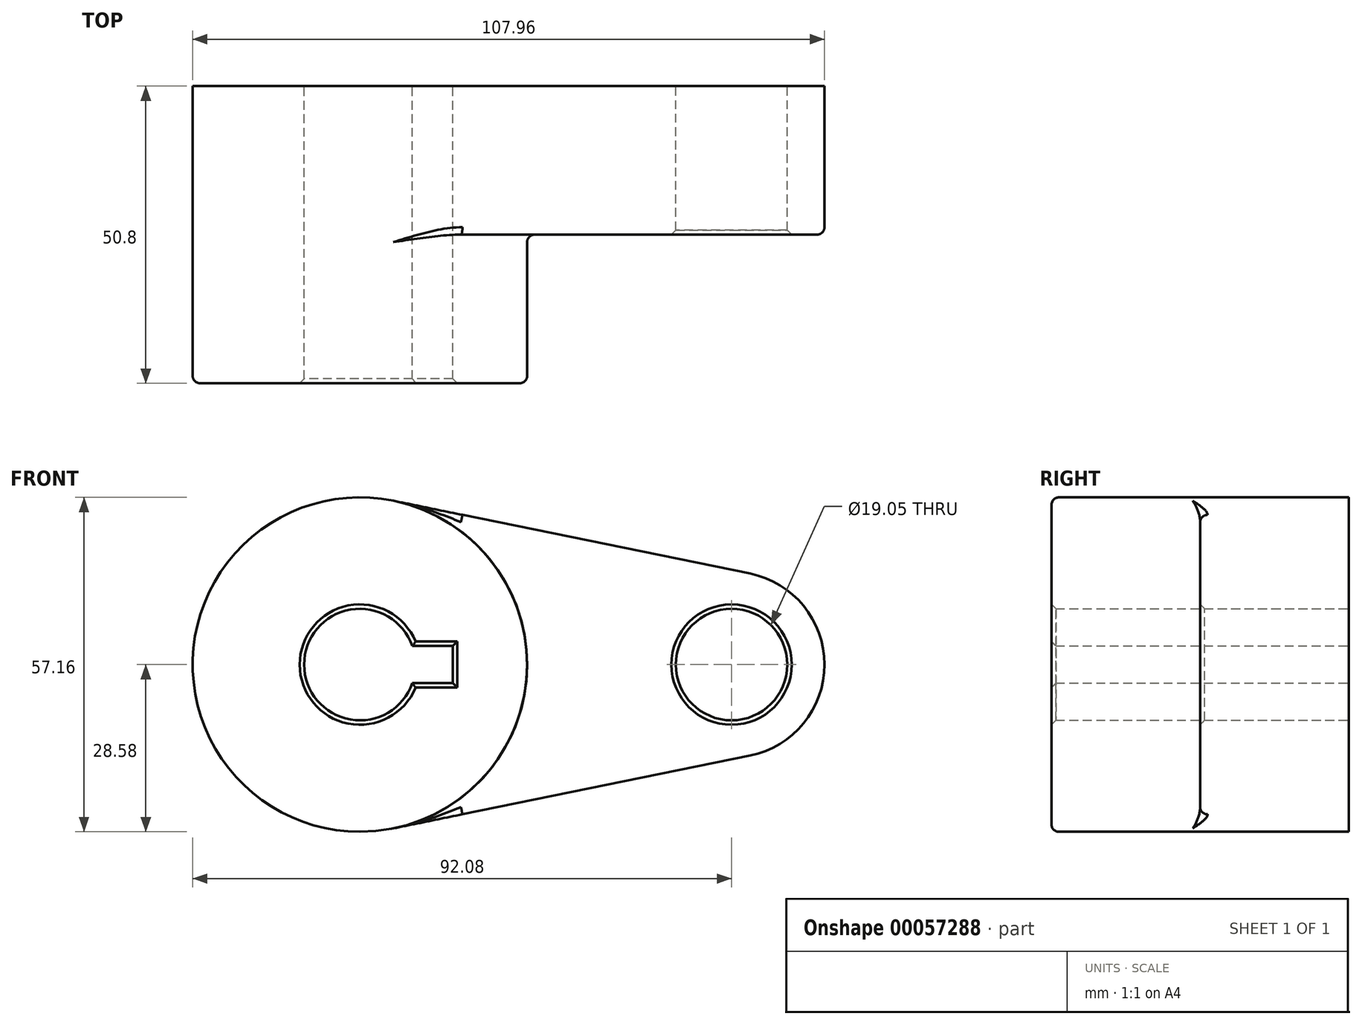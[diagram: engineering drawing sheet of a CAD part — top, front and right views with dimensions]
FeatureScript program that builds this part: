
annotation { "Feature Type Name" : "Feature", "Feature Type Description" : "" }
export const myFeature = defineFeature(function(context is Context, id is Id, definition is map)
    precondition{}
    {
        {
            var Q0;
            Q0=qCreatedBy(makeId("Front.planeOp"),FACE);
            var sketch = newSketch(context, id + "F0", { "sketchPlane" : qUnion([Q0])});
            skCircle(sketch, "E0", {"center": v(0, 0) * mm, "radius": 28.58 * mm});
            skCircle(sketch, "E1", {"center": v(63.5, 0) * mm, "radius": 15.88 * mm});
            skLineSegment(sketch, "E2", {"start": v(5.71, 28) * mm, "end": v(66.68, 15.55) * mm});
            skLineSegment(sketch, "E3", {"start": v(5.71, -28) * mm, "end": v(66.68, -15.55) * mm});
            skCircle(sketch, "E4", {"center": v(0, 0) * mm, "radius": 9.53 * mm});
            skCircle(sketch, "E5", {"center": v(63.5, 0) * mm, "radius": 9.53 * mm});
            skLineSegment(sketch, "E6.rect.bottom", {"start": v(-15.88, 3.17) * mm, "end": v(15.88, 3.17) * mm});
            skLineSegment(sketch, "E6.rect.top", {"start": v(-15.88, -3.17) * mm, "end": v(15.88, -3.17) * mm});
            skLineSegment(sketch, "E6.rect.left", {"start": v(-15.88, 3.17) * mm, "end": v(-15.88, -3.17) * mm});
            skLineSegment(sketch, "E6.rect.right", {"start": v(15.88, 3.17) * mm, "end": v(15.88, -3.17) * mm});
            skSolve(sketch);
        }
        {
            var Q0;
            {var subQ11=sQuery(id+"F0.wireOp",EDGE,"E6.rect.left");Q0=makeQuery(id+"F0.imprint","IMPRINT",FACE,{"disambiguationData":[TD([[makeQuery(id+"F0.imprint","IMPRINT",EDGE,{"derivedFrom":subQ11}),-1.0]])]});}
            var Q1;
            Q1=makeQuery(id+"F0.imprint","IMPRINT",FACE,{"disambiguationData":[TD([[makeQuery(id+"F0.imprint","IMPRINT",EDGE,{"derivedFrom":sQuery(id+"F0.wireOp",EDGE,"E5")}),-1.0]])]});
            var Q2;
            {var subQ0=sQuery(id+"F0.wireOp",EDGE,"E2");Q2=makeQuery(id+"F0.imprint","IMPRINT",FACE,{"disambiguationData":[TD([[makeQuery(id+"F0.imprint","IMPRINT",EDGE,{"derivedFrom":subQ0}),-1.0]])]});}
            var Q3;
            {var subQ5=sQuery(id+"F0.wireOp",EDGE,"E6.rect.left");Q3=makeQuery(id+"F0.imprint","IMPRINT",FACE,{"disambiguationData":[TD([[makeQuery(id+"F0.imprint","IMPRINT",EDGE,{"derivedFrom":subQ5}),1.0]])]});}
            extrude(context, id + "F1", {"entities" : qUnion([Q0, Q1, Q2, Q3]), "depth" : 25.4 * mm});
        }
        {
            var Q0;
            {var subQ11=sQuery(id+"F0.wireOp",EDGE,"E6.rect.left");Q0=makeQuery(id+"F0.imprint","IMPRINT",FACE,{"disambiguationData":[TD([[makeQuery(id+"F0.imprint","IMPRINT",EDGE,{"derivedFrom":subQ11}),-1.0]])]});}
            var Q1;
            {var subQ5=sQuery(id+"F0.wireOp",EDGE,"E6.rect.left");Q1=makeQuery(id+"F0.imprint","IMPRINT",FACE,{"disambiguationData":[TD([[makeQuery(id+"F0.imprint","IMPRINT",EDGE,{"derivedFrom":subQ5}),1.0]])]});}
            extrude(context, id + "F2", {"entities" : qUnion([Q0, Q1]), "operationType" : NewBodyOperationType.ADD, "depth" : 50.8 * mm});
        }
        {
            var Q0;
            {var subQ0=sQuery(id+"F0.wireOp",EDGE,"E0");Q0=makeQuery(id+"F2.boolean.opBoolean","INTERSECT",EDGE,{"derivedFrom":[makeQuery(id+"F1.opExtrude","CAP_FACE",FACE,{"disambiguationData":[OSD([subQ0,sQuery(id+"F0.wireOp",EDGE,"E1"),sQuery(id+"F0.wireOp",EDGE,"E2"),sQuery(id+"F0.wireOp",EDGE,"E3"),sQuery(id+"F0.wireOp",EDGE,"E4"),sQuery(id+"F0.wireOp",EDGE,"E5"),sQuery(id+"F0.wireOp",EDGE,"E6.rect.bottom"),sQuery(id+"F0.wireOp",EDGE,"E6.rect.top"),sQuery(id+"F0.wireOp",EDGE,"E6.rect.right")])],"isStart":false}),makeQuery(id+"F2.opExtrude","SWEPT_FACE",FACE,{"disambiguationData":[OSD([subQ0])]})]});}
            fillet(context, id + "F3", {"entities" : qUnion([Q0]), "radius" : 1.27 * mm, "tangentPropagation" : true, "allowEdgeOverflow" : false});
        }
        {
            var Q0;
            Q0=makeQuery(id+"F1.opExtrude","CAP_EDGE",EDGE,{"disambiguationData":[OSD([sQuery(id+"F0.wireOp",EDGE,"E3")])],"isStart":false});
            fillet(context, id + "F4", {"entities" : qUnion([Q0]), "radius" : 1.27 * mm, "tangentPropagation" : true, "allowEdgeOverflow" : false});
        }
        {
            var Q0;
            Q0=makeQuery(id+"F2.opExtrude","CAP_EDGE",EDGE,{"disambiguationData":[OSD([sQuery(id+"F0.wireOp",EDGE,"E0")])],"isStart":false});
            fillet(context, id + "F5", {"entities" : qUnion([Q0]), "radius" : 1.27 * mm, "tangentPropagation" : true, "allowEdgeOverflow" : false});
        }
        {
            var Q0;
            Q0=makeQuery(id+"F1.opExtrude","CAP_EDGE",EDGE,{"disambiguationData":[OSD([sQuery(id+"F0.wireOp",EDGE,"E5")])],"isStart":false});
            chamfer(context, id + "F6", {"entities" : qUnion([Q0]), "width" : 0.76 * mm, "tangentPropagation" : true});
        }
        {
            var Q0;
            Q0=makeQuery(id+"F2.opExtrude","CAP_EDGE",EDGE,{"disambiguationData":[OSD([sQuery(id+"F0.wireOp",EDGE,"E4")])],"isStart":false});
            var Q1;
            Q1=makeQuery(id+"F2.opExtrude","CAP_EDGE",EDGE,{"disambiguationData":[OSD([sQuery(id+"F0.wireOp",EDGE,"E6.rect.bottom")])],"isStart":false});
            var Q2;
            Q2=makeQuery(id+"F2.opExtrude","CAP_EDGE",EDGE,{"disambiguationData":[OSD([sQuery(id+"F0.wireOp",EDGE,"E6.rect.right")])],"isStart":false});
            var Q3;
            Q3=makeQuery(id+"F2.opExtrude","CAP_EDGE",EDGE,{"disambiguationData":[OSD([sQuery(id+"F0.wireOp",EDGE,"E6.rect.top")])],"isStart":false});
            chamfer(context, id + "F7", {"entities" : qUnion([Q0, Q1, Q2, Q3]), "width" : 0.76 * mm, "tangentPropagation" : true});
        }
    });
